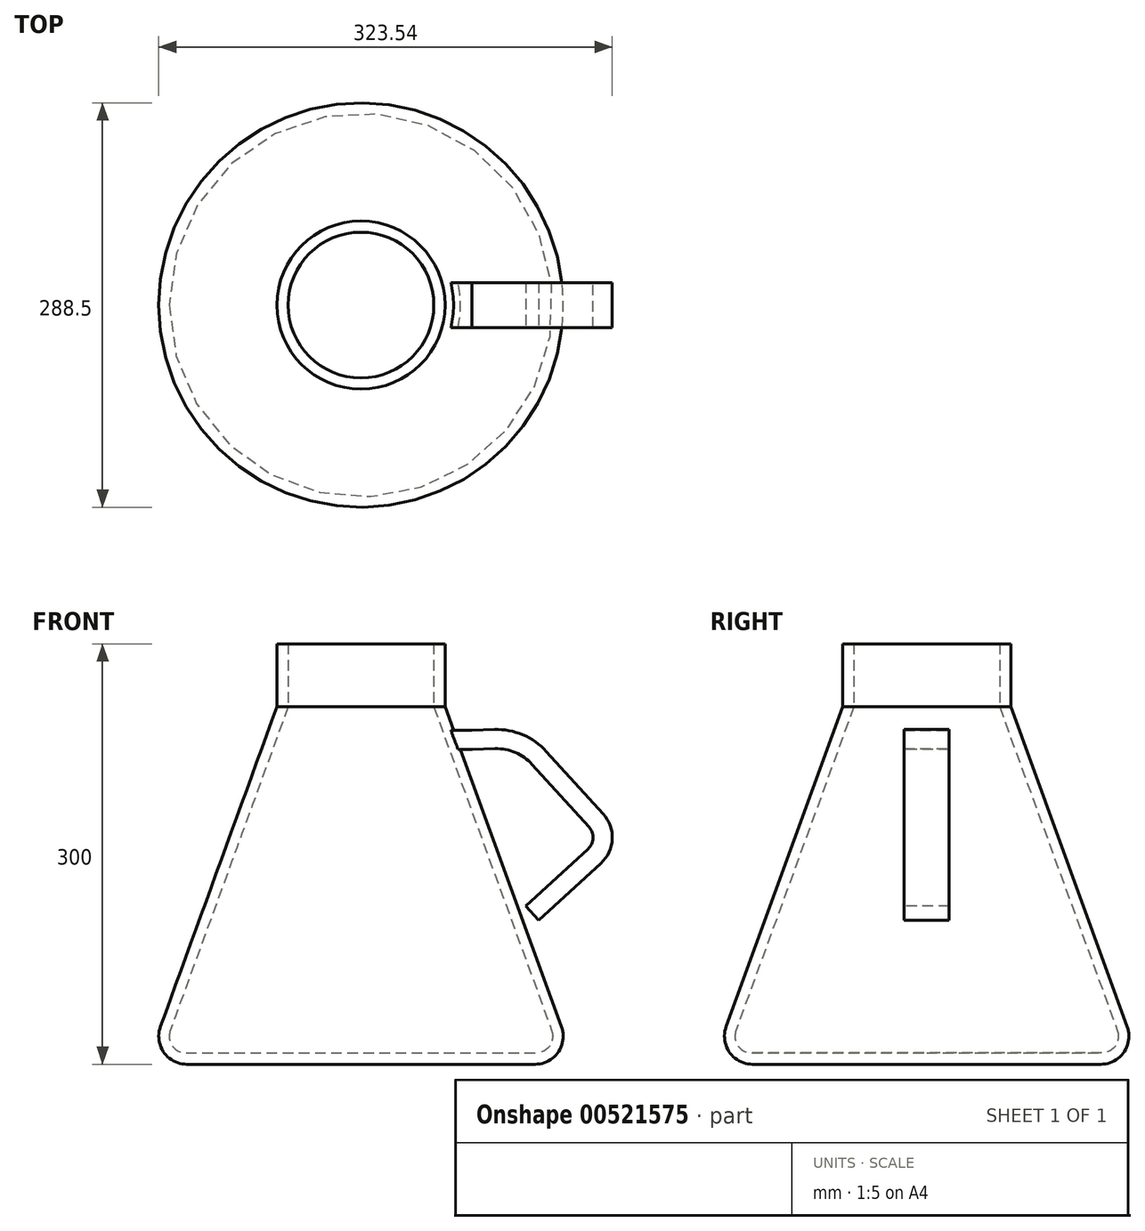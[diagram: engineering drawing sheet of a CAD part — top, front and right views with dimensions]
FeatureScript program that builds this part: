
annotation { "Feature Type Name" : "Feature", "Feature Type Description" : "" }
export const myFeature = defineFeature(function(context is Context, id is Id, definition is map)
    precondition{}
    {
        {
            var Q0;
            Q0=qCreatedBy(makeId("Front.planeOp"),FACE);
            var sketch = newSketch(context, id + "F0", { "sketchPlane" : qUnion([Q0])});
            skLineSegment(sketch, "E0", {"start": v(60, 300) * mm, "end": v(60, 255) * mm});
            skLineSegment(sketch, "E1", {"start": v(60, 255) * mm, "end": v(143.04, 26.84) * mm});
            skLineSegment(sketch, "E2", {"start": v(124.25, 0) * mm, "end": v(0, 0) * mm});
            skLineSegment(sketch, "E3", {"start": v(0, 0) * mm, "end": v(0, 8) * mm});
            skLineSegment(sketch, "E4", {"start": v(0, 8) * mm, "end": v(124.76, 8) * mm});
            skLineSegment(sketch, "E5", {"start": v(136.04, 24.1) * mm, "end": v(52, 255) * mm});
            skLineSegment(sketch, "E6", {"start": v(52, 255) * mm, "end": v(52, 300) * mm});
            skLineSegment(sketch, "E7", {"start": v(52, 300) * mm, "end": v(60, 300) * mm});
            skPoint(sketch, "E8.visualSharp", {"position": v(141.9, 8) * mm});
            skPoint(sketch, "E9.visualSharp", {"position": v(152.81, 0) * mm});
            skArc(sketch, "E9.filletArc", {"start": v(124.25, 0) * mm, "mid": v(140.63, 8.53) * mm, "end": v(143.04, 26.84) * mm});
            skArc(sketch, "E10.filletArc", {"start": v(124.76, 8) * mm, "mid": v(134.6, 13.12) * mm, "end": v(136.04, 24.1) * mm});
            skLineSegment(sketch, "E11", {"start": v(79.5, 201.43) * mm, "end": v(147.28, 226.1) * mm});
            skLineSegment(sketch, "E12", {"start": v(147.28, 226.1) * mm, "end": v(250.12, 152.96) * mm});
            skLineSegment(sketch, "E13", {"start": v(250.12, 152.96) * mm, "end": v(130.03, 62.58) * mm});
            skSolve(sketch);
        }
        {
            var Q0;
            Q0=makeQuery(id+"F0.imprint","IMPRINT",FACE,{"disambiguationData":[TD([[makeQuery(id+"F0.imprint","IMPRINT",EDGE,{"derivedFrom":sQuery(id+"F0.wireOp",EDGE,"E0")}),-1.0]])]});
            var Q1;
            Q1=sQuery(id+"F0.wireOp",EDGE,"E3");
            revolve(context, id + "F1", {"entities" : qUnion([Q0]), "axis" : qUnion([Q1]), "revolveType" : RevolveType.FULL});
        }
        {
            var Q0;
            Q0=qCreatedBy(makeId("Front.planeOp"),FACE);
            var sketch = newSketch(context, id + "F2", { "sketchPlane" : qUnion([Q0])});
            skLineSegment(sketch, "E14", {"start": v(79.23, 233.39) * mm, "end": v(95.43, 233.89) * mm});
            skLineSegment(sketch, "E15", {"start": v(128.56, 219.84) * mm, "end": v(169.06, 175.32) * mm});
            skLineSegment(sketch, "E16", {"start": v(167.73, 147.07) * mm, "end": v(123.27, 106.62) * mm});
            skLineSegment(sketch, "E17", {"start": v(79.23, 233.39) * mm, "end": v(0, 233.39) * mm});
            skPoint(sketch, "E18.visualSharp", {"position": v(182.52, 160.53) * mm});
            skArc(sketch, "E18.filletArc", {"start": v(167.73, 147.07) * mm, "mid": v(174.25, 160.92) * mm, "end": v(169.06, 175.32) * mm});
            skPoint(sketch, "E19.visualSharp", {"position": v(115.23, 234.5) * mm});
            skArc(sketch, "E19.filletArc", {"start": v(128.56, 219.84) * mm, "mid": v(113.53, 230.5) * mm, "end": v(95.43, 233.89) * mm});
            skSolve(sketch);
        }
        {
            var Q0;
            Q0=qCreatedBy(makeId("Right.planeOp"),FACE);
            var sketch = newSketch(context, id + "F3", { "sketchPlane" : qUnion([Q0])});
            skLineSegment(sketch, "E20.bottom", {"start": v(16.02, 238.4) * mm, "end": v(-16.02, 238.4) * mm});
            skLineSegment(sketch, "E20.top", {"start": v(16.02, 224.67) * mm, "end": v(-16.02, 224.67) * mm});
            skLineSegment(sketch, "E20.left", {"start": v(16.02, 238.4) * mm, "end": v(16.02, 224.67) * mm});
            skLineSegment(sketch, "E20.right", {"start": v(-16.02, 238.4) * mm, "end": v(-16.02, 224.67) * mm});
            skPoint(sketch, "E20.middle", {"position": v(0, 231.54) * mm});
            skSolve(sketch);
        }
        {
            var Q0;
            Q0 = qSketchRegion(id + "F3", true);
            var Q1;
            Q1 = qConstructionFilter(qBodyType(qCreatedBy(id + "F2" ,EDGE), BodyType.WIRE), ConstructionObject.NO);
            sweep(context, id + "F4", {"operationType" : NewBodyOperationType.ADD, "profiles" : qUnion([Q0]), "path" : qUnion([Q1])});
        }
        {
            var Q0;
            Q0=makeQuery(id+"F4.opSweep","CAP_FACE",FACE,{"disambiguationData":[OSD([sQuery(id+"F2.wireOp",VERTEX,"E17.end"),sQuery(id+"F3.wireOp",EDGE,"E20.bottom"),sQuery(id+"F3.wireOp",EDGE,"E20.top"),sQuery(id+"F3.wireOp",EDGE,"E20.left"),sQuery(id+"F3.wireOp",EDGE,"E20.right")])],"isStart":true});
            var sketch = newSketch(context, id + "F5", { "sketchPlane" : qUnion([Q0])});
            skLineSegment(sketch, "E21.0", {"start": v(-16.02, 238.4) * mm, "end": v(16.02, 238.4) * mm});
            skLineSegment(sketch, "E22.0", {"start": v(-16.02, 224.67) * mm, "end": v(-16.02, 238.4) * mm});
            skLineSegment(sketch, "E23.0", {"start": v(16.02, 224.67) * mm, "end": v(-16.02, 224.67) * mm});
            skLineSegment(sketch, "E24.0", {"start": v(16.02, 238.4) * mm, "end": v(16.02, 224.67) * mm});
            skSolve(sketch);
        }
        {
            var Q0;
            Q0 = qSketchRegion(id + "F5", true);
            var Q1;
            Q1=makeQuery(id+"F1.opRevolve","SWEPT_FACE",FACE,{"disambiguationData":[OSD([sQuery(id+"F0.wireOp",EDGE,"E5")])]});
            extrude(context, id + "F6", {"entities" : qUnion([Q0]), "operationType" : NewBodyOperationType.REMOVE, "endBound" : BoundingType.UP_TO_SURFACE, "oppositeDirection" : true, "depth" : 25 * mm, "endBoundEntityFace" : qUnion([Q1]), "offsetDistance" : 25 * mm});
        }
    });
